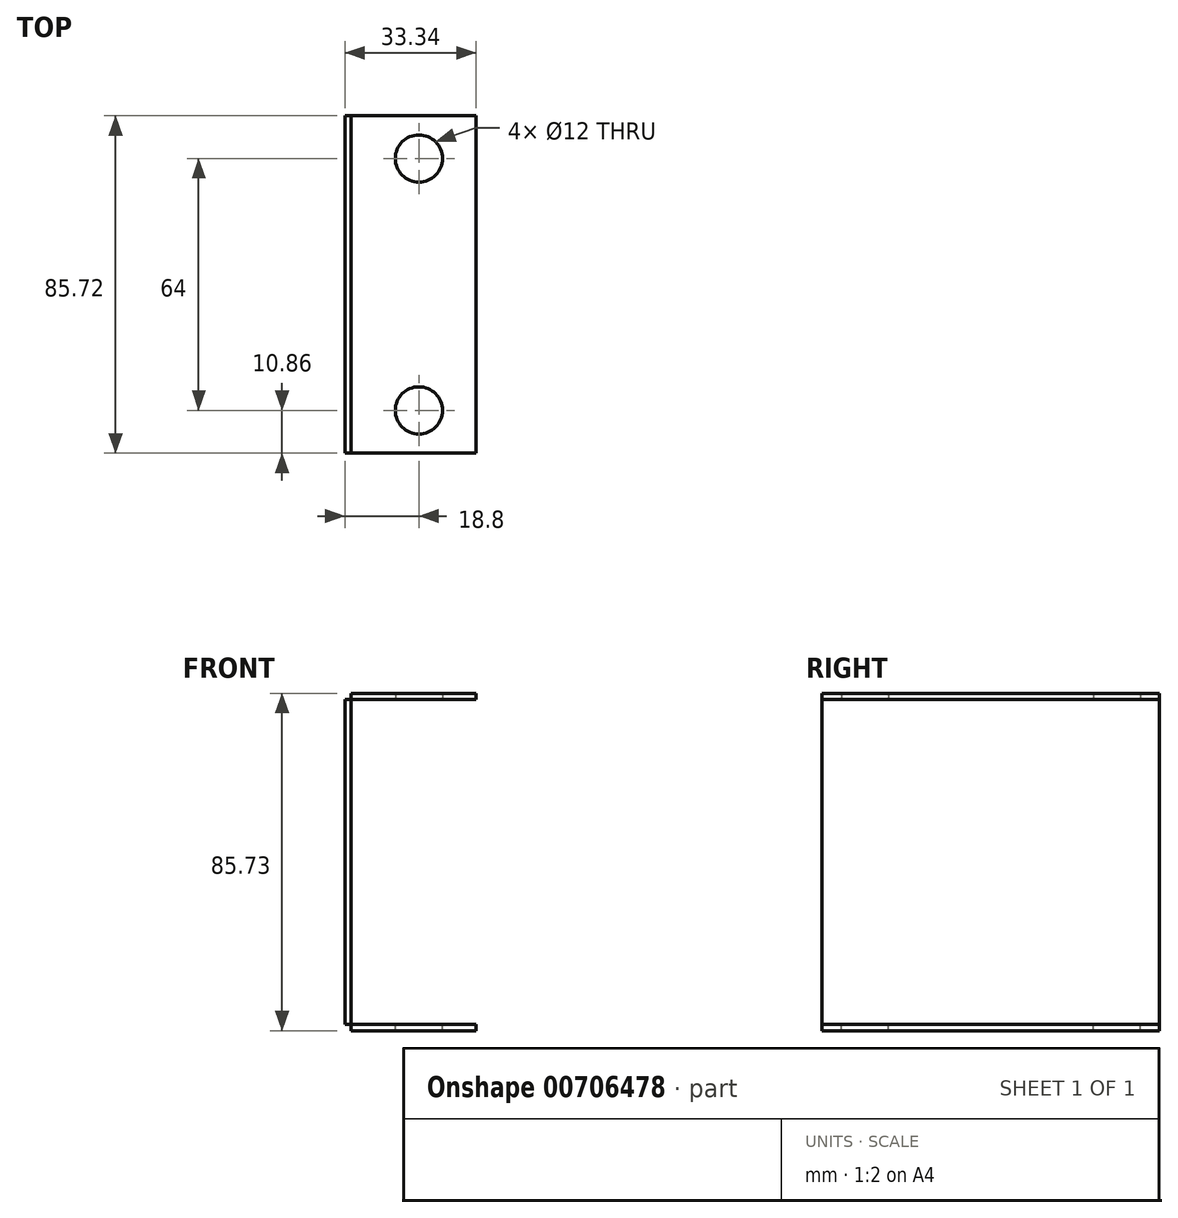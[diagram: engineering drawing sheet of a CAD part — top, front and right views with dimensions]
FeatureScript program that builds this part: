
annotation { "Feature Type Name" : "Feature", "Feature Type Description" : "" }
export const myFeature = defineFeature(function(context is Context, id is Id, definition is map)
    precondition{}
    {
        {
            var Q0;
            Q0=qCreatedBy(makeId("Top.planeOp"),FACE);
            var sketch = newSketch(context, id + "F0", { "sketchPlane" : qUnion([Q0])});
            skCircle(sketch, "E0", {"center": v(-70.22, 12.75) * mm, "radius": 12.7 * mm});
            skCircle(sketch, "E1", {"center": v(-70.22, 12.75) * mm, "radius": 9.53 * mm});
            skCircle(sketch, "E2", {"center": v(-102.23, 44.75) * mm, "radius": 6 * mm});
            skCircle(sketch, "E3", {"center": v(-38.22, 44.75) * mm, "radius": 6 * mm, "construction": true});
            skCircle(sketch, "E4", {"center": v(-38.22, -19.25) * mm, "radius": 6 * mm, "construction": true});
            skCircle(sketch, "E5", {"center": v(-102.23, -19.25) * mm, "radius": 6 * mm});
            skCircle(sketch, "E6", {"center": v(-102.23, 44.75) * mm, "radius": 4 * mm, "construction": true});
            skCircle(sketch, "E7", {"center": v(-38.22, 44.75) * mm, "radius": 4 * mm});
            skCircle(sketch, "E8", {"center": v(-102.23, -19.25) * mm, "radius": 4 * mm, "construction": true});
            skCircle(sketch, "E9", {"center": v(-38.22, -19.25) * mm, "radius": 4 * mm});
            skLineSegment(sketch, "E10.bottom", {"start": v(-113.09, 55.61) * mm, "end": v(-27.36, 55.61) * mm, "construction": true});
            skLineSegment(sketch, "E10.top", {"start": v(-113.09, -30.11) * mm, "end": v(-27.36, -30.11) * mm, "construction": true});
            skLineSegment(sketch, "E10.left", {"start": v(-113.09, 55.61) * mm, "end": v(-113.09, -30.11) * mm, "construction": true});
            skLineSegment(sketch, "E10.right", {"start": v(-27.36, 55.61) * mm, "end": v(-27.36, -30.11) * mm, "construction": true});
            skPoint(sketch, "E11", {"position": v(-70.22, 55.61) * mm});
            skPoint(sketch, "E12", {"position": v(-113.09, 12.75) * mm});
            skLineSegment(sketch, "E13.bottom", {"start": v(-119.44, 55.61) * mm, "end": v(-87.69, 55.61) * mm});
            skLineSegment(sketch, "E13.top", {"start": v(-119.44, -30.11) * mm, "end": v(-87.69, -30.11) * mm});
            skLineSegment(sketch, "E13.left", {"start": v(-119.44, 55.61) * mm, "end": v(-119.44, -30.11) * mm});
            skLineSegment(sketch, "E13.right", {"start": v(-87.69, 55.61) * mm, "end": v(-87.69, -30.11) * mm});
            skLineSegment(sketch, "E14.bottom", {"start": v(-119.44, 55.61) * mm, "end": v(-201.99, 55.61) * mm});
            skLineSegment(sketch, "E14.top", {"start": v(-119.44, -30.11) * mm, "end": v(-201.99, -30.11) * mm});
            skLineSegment(sketch, "E14.right", {"start": v(-201.99, 55.61) * mm, "end": v(-201.99, -30.11) * mm});
            skLineSegment(sketch, "E15.bottom", {"start": v(-233.74, 55.61) * mm, "end": v(-201.99, 55.61) * mm});
            skLineSegment(sketch, "E15.top", {"start": v(-233.74, -30.11) * mm, "end": v(-201.99, -30.11) * mm});
            skLineSegment(sketch, "E15.left", {"start": v(-233.74, 55.61) * mm, "end": v(-233.74, -30.11) * mm});
            skCircle(sketch, "E16", {"center": v(-219.2, 44.75) * mm, "radius": 6 * mm});
            skCircle(sketch, "E17", {"center": v(-219.2, -19.25) * mm, "radius": 6 * mm});
            skLineSegment(sketch, "E18", {"start": v(-102.23, 44.75) * mm, "end": v(-87.69, 44.75) * mm, "construction": true});
            skLineSegment(sketch, "E19", {"start": v(-219.2, 44.75) * mm, "end": v(-233.74, 44.75) * mm, "construction": true});
            skCircle(sketch, "E20", {"center": v(-219.2, 44.75) * mm, "radius": 0.13 * mm});
            skCircle(sketch, "E21", {"center": v(-102.23, 44.75) * mm, "radius": 0.13 * mm});
            skCircle(sketch, "E22", {"center": v(-102.23, -19.25) * mm, "radius": 0.13 * mm});
            skCircle(sketch, "E23", {"center": v(-219.2, -19.25) * mm, "radius": 0.13 * mm});
            skLineSegment(sketch, "E24", {"start": v(-219.2, 44.75) * mm, "end": v(-201.99, 44.75) * mm, "construction": true});
            skSolve(sketch);
        }
        {
            var Q0;
            Q0=makeQuery(id+"F0.imprint","IMPRINT",FACE,{"disambiguationData":[TD([[makeQuery(id+"F0.imprint","IMPRINT",EDGE,{"derivedFrom":sQuery(id+"F0.wireOp",EDGE,"E2")}),-1.0]])]});
            extrude(context, id + "F1", {"entities" : qUnion([Q0]), "depth" : 1.59 * mm, "offsetDistance" : 25.4 * mm});
        }
        {
            var Q0;
            Q0=makeQuery(id+"F0.imprint","IMPRINT",FACE,{"disambiguationData":[TD([[makeQuery(id+"F0.imprint","IMPRINT",EDGE,{"derivedFrom":sQuery(id+"F0.wireOp",EDGE,"E14.bottom")}),1.0]])]});
            extrude(context, id + "F2", {"entities" : qUnion([Q0]), "depth" : 1.59 * mm, "offsetDistance" : 25.4 * mm});
        }
        {
            var Q0;
            Q0=makeQuery(id+"F0.imprint","IMPRINT",FACE,{"disambiguationData":[TD([[makeQuery(id+"F0.imprint","IMPRINT",EDGE,{"derivedFrom":sQuery(id+"F0.wireOp",EDGE,"E15.bottom")}),-1.0]])]});
            extrude(context, id + "F3", {"entities" : qUnion([Q0]), "depth" : 1.59 * mm, "offsetDistance" : 25.4 * mm});
        }
        {
            var Q0;
            Q0=makeQuery(id+"F2.opExtrude","SWEPT_BODY",BODY,{"disambiguationData":[OSD([sQuery(id+"F0.wireOp",EDGE,"E14.bottom"),sQuery(id+"F0.wireOp",EDGE,"E14.top"),sQuery(id+"F0.wireOp",EDGE,"E13.left"),sQuery(id+"F0.wireOp",EDGE,"E14.right")])]});
            var Q1;
            Q1=makeQuery(id+"F1.opExtrude","CAP_EDGE",EDGE,{"disambiguationData":[OSD([sQuery(id+"F0.wireOp",EDGE,"E13.left")])],"isStart":true});
            transform(context, id + "F4", {"entities" : qUnion([Q0]), "transformType" : TransformType.ROTATION, "transformAxis" : qUnion([Q1]), "angle" : 90 * degree, "makeCopy" : false});
        }
        {
            var Q0;
            Q0=makeQuery(id+"F3.opExtrude","SWEPT_BODY",BODY,{"disambiguationData":[OSD([sQuery(id+"F0.wireOp",EDGE,"E15.bottom"),sQuery(id+"F0.wireOp",EDGE,"E15.top"),sQuery(id+"F0.wireOp",EDGE,"E15.left"),sQuery(id+"F0.wireOp",EDGE,"E14.right"),sQuery(id+"F0.wireOp",EDGE,"E16"),sQuery(id+"F0.wireOp",EDGE,"E17")])]});
            var Q1;
            Q1=makeQuery(id+"F3.opExtrude","CAP_EDGE",EDGE,{"disambiguationData":[OSD([sQuery(id+"F0.wireOp",EDGE,"E14.right")])],"isStart":true});
            transform(context, id + "F5", {"entities" : qUnion([Q0]), "transformType" : TransformType.ROTATION, "transformAxis" : qUnion([Q1]), "angle" : 180 * degree, "makeCopy" : false});
        }
        {
            var Q0;
            Q0=makeQuery(id+"F3.opExtrude","SWEPT_BODY",BODY,{"disambiguationData":[OSD([sQuery(id+"F0.wireOp",EDGE,"E15.bottom"),sQuery(id+"F0.wireOp",EDGE,"E15.top"),sQuery(id+"F0.wireOp",EDGE,"E15.left"),sQuery(id+"F0.wireOp",EDGE,"E14.right"),sQuery(id+"F0.wireOp",EDGE,"E16"),sQuery(id+"F0.wireOp",EDGE,"E17")])]});
            transform(context, id + "F6", {"entities" : qUnion([Q0]), "transformType" : TransformType.TRANSLATION_3D, "dx" : 82.55 * mm, "dy" : 0 * mm, "dz" : -82.55 * mm, "makeCopy" : false});
        }
    });
